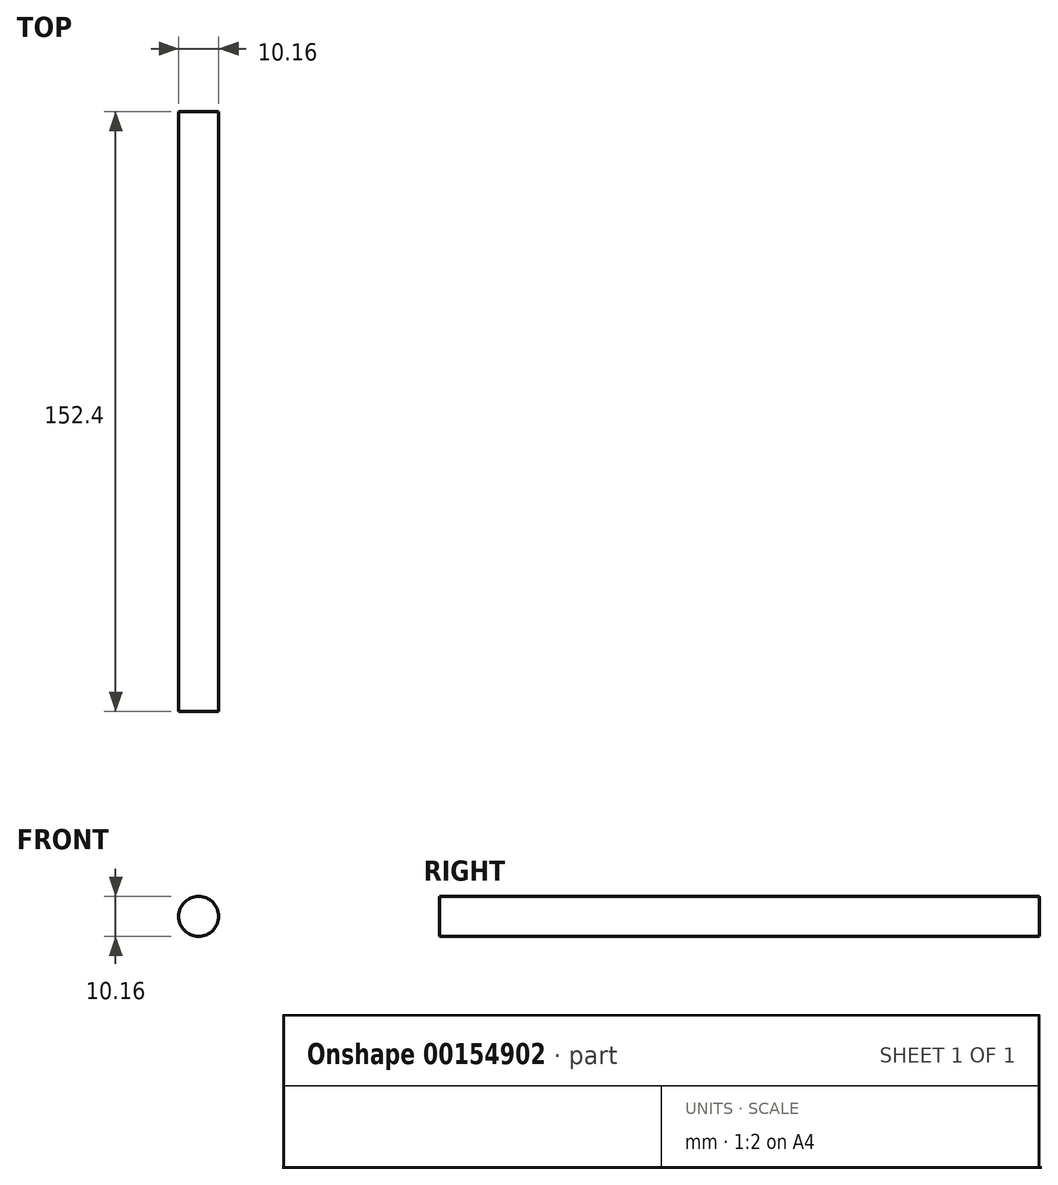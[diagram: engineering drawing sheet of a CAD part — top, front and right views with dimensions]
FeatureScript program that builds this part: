
annotation { "Feature Type Name" : "Feature", "Feature Type Description" : "" }
export const myFeature = defineFeature(function(context is Context, id is Id, definition is map)
    precondition{}
    {
        {
            var Q0;
            Q0=qCreatedBy(makeId("Front.planeOp"),FACE);
            var sketch = newSketch(context, id + "F0", { "sketchPlane" : qUnion([Q0])});
            skCircle(sketch, "E0", {"center": v(0, 0) * mm, "radius": 5.08 * mm});
            skSolve(sketch);
        }
        {
            var Q0;
            Q0=makeQuery(id+"F0.imprint","IMPRINT",FACE,{"disambiguationData":[TD([[makeQuery(id+"F0.imprint","IMPRINT",EDGE,{"derivedFrom":sQuery(id+"F0.wireOp",EDGE,"E0")}),1.0]])]});
            extrude(context, id + "F1", {"entities" : qUnion([Q0]), "depth" : 152.4 * mm});
        }
    });
